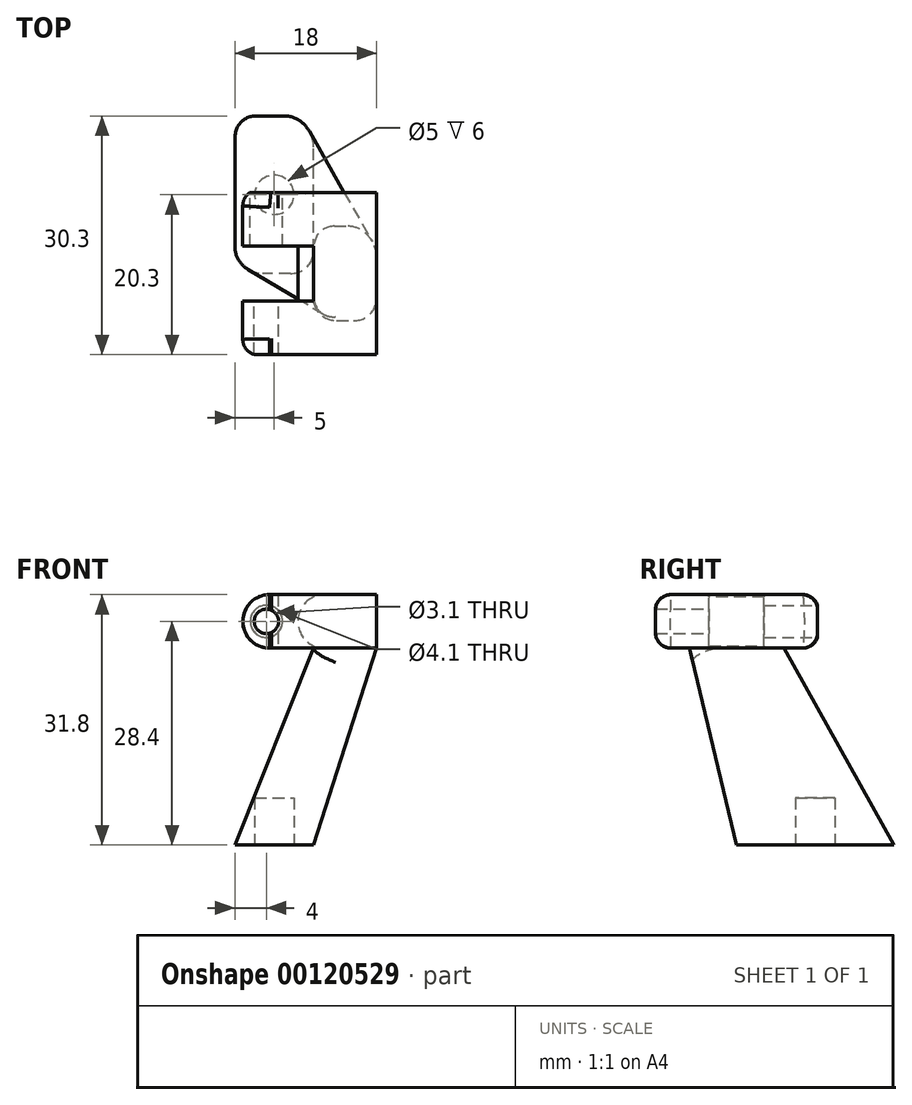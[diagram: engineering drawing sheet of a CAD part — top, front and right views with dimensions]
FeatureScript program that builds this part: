
annotation { "Feature Type Name" : "Feature", "Feature Type Description" : "" }
export const myFeature = defineFeature(function(context is Context, id is Id, definition is map)
    precondition{}
    {
        {
            var Q0;
            Q0=qCreatedBy(makeId("Top.planeOp"),FACE);
            var sketch = newSketch(context, id + "F0", { "sketchPlane" : qUnion([Q0])});
            skLineSegment(sketch, "E0", {"start": v(0, -10.3) * mm, "end": v(-2, -10.3) * mm});
            skLineSegment(sketch, "E1", {"start": v(-2, -10.3) * mm, "end": v(-9, -10.3) * mm});
            skLineSegment(sketch, "E2", {"start": v(-9, -10.3) * mm, "end": v(-9, -3.5) * mm});
            skLineSegment(sketch, "E3", {"start": v(-9, -3.5) * mm, "end": v(-2, -3.5) * mm});
            skLineSegment(sketch, "E4", {"start": v(-2, -3.5) * mm, "end": v(-2, 0) * mm});
            skPoint(sketch, "E5", {"position": v(-2, 0) * mm});
            skLineSegment(sketch, "E6.MirrorCS", {"start": v(-2, 3.5) * mm, "end": v(-2, 0) * mm});
            skLineSegment(sketch, "E7.MirrorCS", {"start": v(-9, 10.3) * mm, "end": v(-9, 3.5) * mm});
            skLineSegment(sketch, "E8.MirrorCS", {"start": v(-9, 3.5) * mm, "end": v(-2, 3.5) * mm});
            skLineSegment(sketch, "E9.MirrorCS", {"start": v(0, 10.3) * mm, "end": v(-2, 10.3) * mm});
            skLineSegment(sketch, "E10.MirrorCS", {"start": v(-2, 10.3) * mm, "end": v(-9, 10.3) * mm});
            skLineSegment(sketch, "E11", {"start": v(0, -10.3) * mm, "end": v(0, 10.3) * mm});
            skPoint(sketch, "E12.orphan", {"position": v(0, 23.14) * mm});
            skPoint(sketch, "E13.orphan", {"position": v(0, -34.54) * mm});
            skPoint(sketch, "E14.MirrorCS.end.orphan", {"position": v(0, -19.04) * mm});
            skPoint(sketch, "E15.start.orphan", {"position": v(2.04, -21.24) * mm});
            skPoint(sketch, "E16.orphan", {"position": v(24.85, 0) * mm});
            skLineSegment(sketch, "E17.bottom", {"start": v(0, -10.3) * mm, "end": v(8, -10.3) * mm});
            skLineSegment(sketch, "E17.top", {"start": v(0, 10.3) * mm, "end": v(8, 10.3) * mm});
            skLineSegment(sketch, "E17.right", {"start": v(8, -10.3) * mm, "end": v(8, 10.3) * mm});
            skSolve(sketch);
        }
        {
            var Q0;
            Q0=makeQuery(id+"F0.imprint","IMPRINT",FACE,{"disambiguationData":[TD([[makeQuery(id+"F0.imprint","IMPRINT",EDGE,{"derivedFrom":sQuery(id+"F0.wireOp",EDGE,"zT8ULMTL-c5zF-14Nq-p09k-rvLnDzIjeo5f")}),-1.0]])]});
            var Q1;
            {var subQ1=sQuery(id+"F0.wireOp",EDGE,"E1");Q1=makeQuery(id+"F0.imprint","IMPRINT",FACE,{"disambiguationData":[TD([[makeQuery(id+"F0.imprint","IMPRINT",EDGE,{"derivedFrom":subQ1}),-1.0]])]});}
            var Q2;
            {var subQ0=sQuery(id+"F0.wireOp",EDGE,"E15");Q2=makeQuery(id+"F0.imprint","IMPRINT",FACE,{"disambiguationData":[TD([[makeQuery(id+"F0.imprint","IMPRINT",EDGE,{"derivedFrom":subQ0}),1.0]])]});}
            extrude(context, id + "F1", {"entities" : qUnion([Q0, Q1, Q2]), "depth" : 6.8 * mm});
        }
        {
            var Q0;
            Q0=makeQuery(id+"F1.opExtrude","CAP_EDGE",EDGE,{"disambiguationData":[OSD([sQuery(id+"F0.wireOp",EDGE,"E7.MirrorCS")])],"isStart":false});
            var Q1;
            Q1=makeQuery(id+"F1.opExtrude","CAP_EDGE",EDGE,{"disambiguationData":[OSD([sQuery(id+"F0.wireOp",EDGE,"E7.MirrorCS")])],"isStart":true});
            var Q2;
            Q2=makeQuery(id+"F1.opExtrude","CAP_EDGE",EDGE,{"disambiguationData":[OSD([sQuery(id+"F0.wireOp",EDGE,"E2")])],"isStart":true});
            var Q3;
            Q3=makeQuery(id+"F1.opExtrude","CAP_EDGE",EDGE,{"disambiguationData":[OSD([sQuery(id+"F0.wireOp",EDGE,"E2")])],"isStart":false});
            var Q4;
            Q4=makeQuery(id+"F1.opExtrude","CAP_EDGE",EDGE,{"disambiguationData":[OSD([sQuery(id+"F0.wireOp",EDGE,"E4"),sQuery(id+"F0.wireOp",EDGE,"E6.MirrorCS")])],"isStart":true});
            var Q5;
            Q5=makeQuery(id+"F1.opExtrude","CAP_EDGE",EDGE,{"disambiguationData":[OSD([sQuery(id+"F0.wireOp",EDGE,"E4"),sQuery(id+"F0.wireOp",EDGE,"E6.MirrorCS")])],"isStart":false});
            fillet(context, id + "F2", {"entities" : qUnion([Q0, Q1, Q2, Q3, Q4, Q5]), "radius" : 6.8 * mm / 2, "tangentPropagation" : true, "allowEdgeOverflow" : false});
        }
        {
            var Q0;
            Q0=makeQuery(id+"F1.opExtrude","SWEPT_FACE",FACE,{"disambiguationData":[OSD([sQuery(id+"F0.wireOp",EDGE,"E10.MirrorCS")])]});
            var sketch = newSketch(context, id + "F3", { "sketchPlane" : qUnion([Q0])});
            skLineSegment(sketch, "E18", {"start": v(5.6, 0) * mm, "end": v(5.6, 6.8) * mm, "construction": true});
            skPoint(sketch, "E19", {"position": v(6, 3.4) * mm});
            skCircle(sketch, "E20", {"center": v(6, 3.4) * mm, "radius": 2.05 * mm});
            skCircle(sketch, "E21", {"center": v(6, 3.4) * mm, "radius": 1.55 * mm});
            skLineSegment(sketch, "E22", {"start": v(6, 6.78) * mm, "end": v(6, 0.02) * mm, "construction": true});
            skSolve(sketch);
        }
        {
            var Q0;
            Q0=makeQuery(id+"F3.imprint","IMPRINT",FACE,{"disambiguationData":[TD([[makeQuery(id+"F3.imprint","IMPRINT",EDGE,{"derivedFrom":sQuery(id+"F3.wireOp",EDGE,"E21")}),1.0]])]});
            extrude(context, id + "F4", {"entities" : qUnion([Q0]), "operationType" : NewBodyOperationType.REMOVE, "endBound" : BoundingType.THROUGH_ALL, "oppositeDirection" : true, "depth" : 25 * mm});
        }
        {
            var Q0;
            Q0=makeQuery(id+"F3.imprint","IMPRINT",FACE,{"disambiguationData":[TD([[makeQuery(id+"F3.imprint","IMPRINT",EDGE,{"derivedFrom":sQuery(id+"F3.wireOp",EDGE,"E20")}),1.0]])]});
            extrude(context, id + "F5", {"entities" : qUnion([Q0]), "operationType" : NewBodyOperationType.REMOVE, "oppositeDirection" : true, "depth" : 7 * mm});
        }
        {
            var Q0;
            Q0=makeQuery(id+"F0.imprint","IMPRINT",FACE,{"disambiguationData":[TD([[makeQuery(id+"F0.imprint","IMPRINT",EDGE,{"derivedFrom":sQuery(id+"F0.wireOp",EDGE,"E17.bottom")}),1.0]])]});
            var Q1;
            Q1=makeQuery(id+"F1.opExtrude","CAP_FACE",FACE,{"disambiguationData":[OSD([sQuery(id+"F0.wireOp",EDGE,"E0"),sQuery(id+"F0.wireOp",EDGE,"E1"),sQuery(id+"F0.wireOp",EDGE,"E2"),sQuery(id+"F0.wireOp",EDGE,"E3"),sQuery(id+"F0.wireOp",EDGE,"E4"),sQuery(id+"F0.wireOp",EDGE,"E6.MirrorCS"),sQuery(id+"F0.wireOp",EDGE,"E7.MirrorCS"),sQuery(id+"F0.wireOp",EDGE,"E8.MirrorCS"),sQuery(id+"F0.wireOp",EDGE,"E9.MirrorCS"),sQuery(id+"F0.wireOp",EDGE,"E10.MirrorCS"),sQuery(id+"F0.wireOp",EDGE,"Wm3jARsY-aOFY-taCI-q56u-3gJQePx0DChd")])],"isStart":false});
            extrude(context, id + "F6", {"entities" : qUnion([Q0]), "operationType" : NewBodyOperationType.ADD, "endBound" : BoundingType.UP_TO_SURFACE, "endBoundEntityFace" : qUnion([Q1]), "depth" : 25 * mm, "offsetDistance" : 25 * mm});
        }
        {
            var Q0;
            Q0=makeQuery(id+"F1.opExtrude","CAP_EDGE",EDGE,{"disambiguationData":[OSD([sQuery(id+"F0.wireOp",EDGE,"E9.MirrorCS")])],"isStart":true});
            var Q1;
            Q1=makeQuery(id+"F1.opExtrude","CAP_EDGE",EDGE,{"disambiguationData":[OSD([sQuery(id+"F0.wireOp",EDGE,"E0")])],"isStart":true});
            fillet(context, id + "F7", {"entities" : qUnion([Q0, Q1]), "radius" : 2 * mm, "tangentPropagation" : true, "allowEdgeOverflow" : false});
        }
        {
            var Q0;
            Q0=makeQuery(id+"F0.imprint","IMPRINT",FACE,{"disambiguationData":[TD([[makeQuery(id+"F0.imprint","IMPRINT",EDGE,{"derivedFrom":sQuery(id+"F0.wireOp",EDGE,"E17.bottom")}),1.0]])]});
            var sketch = newSketch(context, id + "F8", { "sketchPlane" : qUnion([Q0])});
            skLineSegment(sketch, "E23.top", {"start": v(0, -6) * mm, "end": v(8, -6) * mm});
            skLineSegment(sketch, "E24.top", {"start": v(0, 6) * mm, "end": v(8, 6) * mm});
            skLineSegment(sketch, "E25", {"start": v(8, -6) * mm, "end": v(8, 6) * mm});
            skLineSegment(sketch, "E26", {"start": v(0, -6) * mm, "end": v(0, 6) * mm});
            skSolve(sketch);
        }
        {
            var Q0;
            Q0=makeQuery(id+"F8.imprint","IMPRINT",FACE,{"disambiguationData":[TD([[makeQuery(id+"F8.imprint","IMPRINT",EDGE,{"derivedFrom":sQuery(id+"F8.wireOp",EDGE,"E23.top")}),1.0]])]});
            cPlane(context, id + "F9", {"entities" : qUnion([Q0]), "cplaneType" : CPlaneType.OFFSET, "offset" : 25 * mm, "oppositeDirection" : true, "width" : 150 * mm, "height" : 150 * mm});
        }
        {
            var Q0;
            Q0=qCreatedBy(id+"F9.planeOp",FACE);
            var sketch = newSketch(context, id + "F10", { "sketchPlane" : qUnion([Q0])});
            skLineSegment(sketch, "E27.bottom", {"start": v(0, 0) * mm, "end": v(-10, 0) * mm});
            skLineSegment(sketch, "E27.top", {"start": v(0, 20) * mm, "end": v(-10, 20) * mm});
            skLineSegment(sketch, "E27.left", {"start": v(0, 0) * mm, "end": v(0, 20) * mm});
            skLineSegment(sketch, "E27.right", {"start": v(-10, 0) * mm, "end": v(-10, 20) * mm});
            skSolve(sketch);
        }
        {
            var Q1;
            Q1=makeQuery(id+"F10.imprint","IMPRINT",FACE,{"disambiguationData":[TD([[makeQuery(id+"F10.imprint","IMPRINT",EDGE,{"derivedFrom":sQuery(id+"F10.wireOp",EDGE,"E27.bottom")}),-1.0]])]});
            var Q2;
            Q2=makeQuery(id+"F8.imprint","IMPRINT",FACE,{"disambiguationData":[TD([[makeQuery(id+"F8.imprint","IMPRINT",EDGE,{"derivedFrom":sQuery(id+"F8.wireOp",EDGE,"E23.top")}),1.0]])]});
            loft(context, id + "F11", {"operationType" : NewBodyOperationType.ADD, "sheetProfilesArray" : [{ "sheetProfileEntities" : qUnion([Q1]) }, { "sheetProfileEntities" : qUnion([Q2]) }]});
        }
        {
            var Q0;
            Q0=makeQuery(id+"F11.opLoft","SWEPT_EDGE",EDGE,{"disambiguationData":[OSD([sQuery(id+"F0.wireOp",EDGE,"E11"),sQuery(id+"F8.wireOp",EDGE,"E24.top"),sQuery(id+"F8.wireOp",EDGE,"E26"),sQuery(id+"F10.wireOp",EDGE,"E27.top"),sQuery(id+"F10.wireOp",EDGE,"E27.right")])]});
            var Q1;
            Q1=makeQuery(id+"F11.opLoft","SWEPT_EDGE",EDGE,{"disambiguationData":[OSD([sQuery(id+"F0.wireOp",EDGE,"E11"),sQuery(id+"F8.wireOp",EDGE,"E23.top"),sQuery(id+"F8.wireOp",EDGE,"E26"),sQuery(id+"F10.wireOp",EDGE,"E27.bottom"),sQuery(id+"F10.wireOp",EDGE,"E27.right")])]});
            var Q2;
            Q2=makeQuery(id+"F11.opLoft","SWEPT_EDGE",EDGE,{"disambiguationData":[OSD([sQuery(id+"F0.wireOp",EDGE,"E17.right"),sQuery(id+"F8.wireOp",EDGE,"E23.top"),sQuery(id+"F8.wireOp",EDGE,"E25"),sQuery(id+"F10.wireOp",EDGE,"E27.bottom"),sQuery(id+"F10.wireOp",EDGE,"E27.left")])]});
            var Q3;
            Q3=makeQuery(id+"F11.opLoft","SWEPT_EDGE",EDGE,{"disambiguationData":[OSD([sQuery(id+"F0.wireOp",EDGE,"E17.right"),sQuery(id+"F8.wireOp",EDGE,"E24.top"),sQuery(id+"F8.wireOp",EDGE,"E25"),sQuery(id+"F10.wireOp",EDGE,"E27.top"),sQuery(id+"F10.wireOp",EDGE,"E27.left")])]});
            fillet(context, id + "F12", {"entities" : qUnion([Q0, Q1, Q2, Q3]), "radius" : 3 * mm, "tangentPropagation" : true, "allowEdgeOverflow" : false});
        }
        {
            var Q0;
            Q0=makeQuery(id+"F11.opLoft","CAP_FACE",FACE,{"disambiguationData":[OSD([makeQuery(id+"F10.imprint","IMPRINT",FACE,{"disambiguationData":[TD([[makeQuery(id+"F10.imprint","IMPRINT",EDGE,{"derivedFrom":sQuery(id+"F10.wireOp",EDGE,"E27.bottom")}),-1.0]])]})])],"isStart":true});
            var sketch = newSketch(context, id + "F13", { "sketchPlane" : qUnion([Q0])});
            skCircle(sketch, "E28", {"center": v(-5, -10) * mm, "radius": 2.5 * mm});
            skSolve(sketch);
        }
        {
            var Q0;
            Q0=makeQuery(id+"F13.imprint","IMPRINT",FACE,{"disambiguationData":[TD([[makeQuery(id+"F13.imprint","IMPRINT",EDGE,{"derivedFrom":sQuery(id+"F13.wireOp",EDGE,"E28")}),1.0]])]});
            extrude(context, id + "F14", {"entities" : qUnion([Q0]), "operationType" : NewBodyOperationType.REMOVE, "oppositeDirection" : true, "depth" : 6 * mm, "offsetDistance" : 25 * mm});
        }
    });
